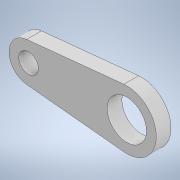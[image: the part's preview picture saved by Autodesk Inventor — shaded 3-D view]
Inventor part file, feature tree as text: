
AUTODESK INVENTOR PART (.ipt)
format: ipt  version: 2022 (Build 260153000, 153)  size: 109,568 bytes
history: native  units: mm
features: other x1, extrude x1, sketch x1
ambient origin geometry x8: Origin, YZ Plane, XZ Plane, XY Plane, X Axis, Y Axis, Z Axis, Center Point
bodies: Body1 (feature_tree)
feature tree (3):
  other  "Sólido1"
  extrude  "Extrusão1"  Depth=15.0mm
  sketch  "Esboço1"  dims[d0=20.0mm d1=40.0mm d2=40.0mm d3=60.0mm d4=100.0mm d5=15.0mm d6=0.0mm]
